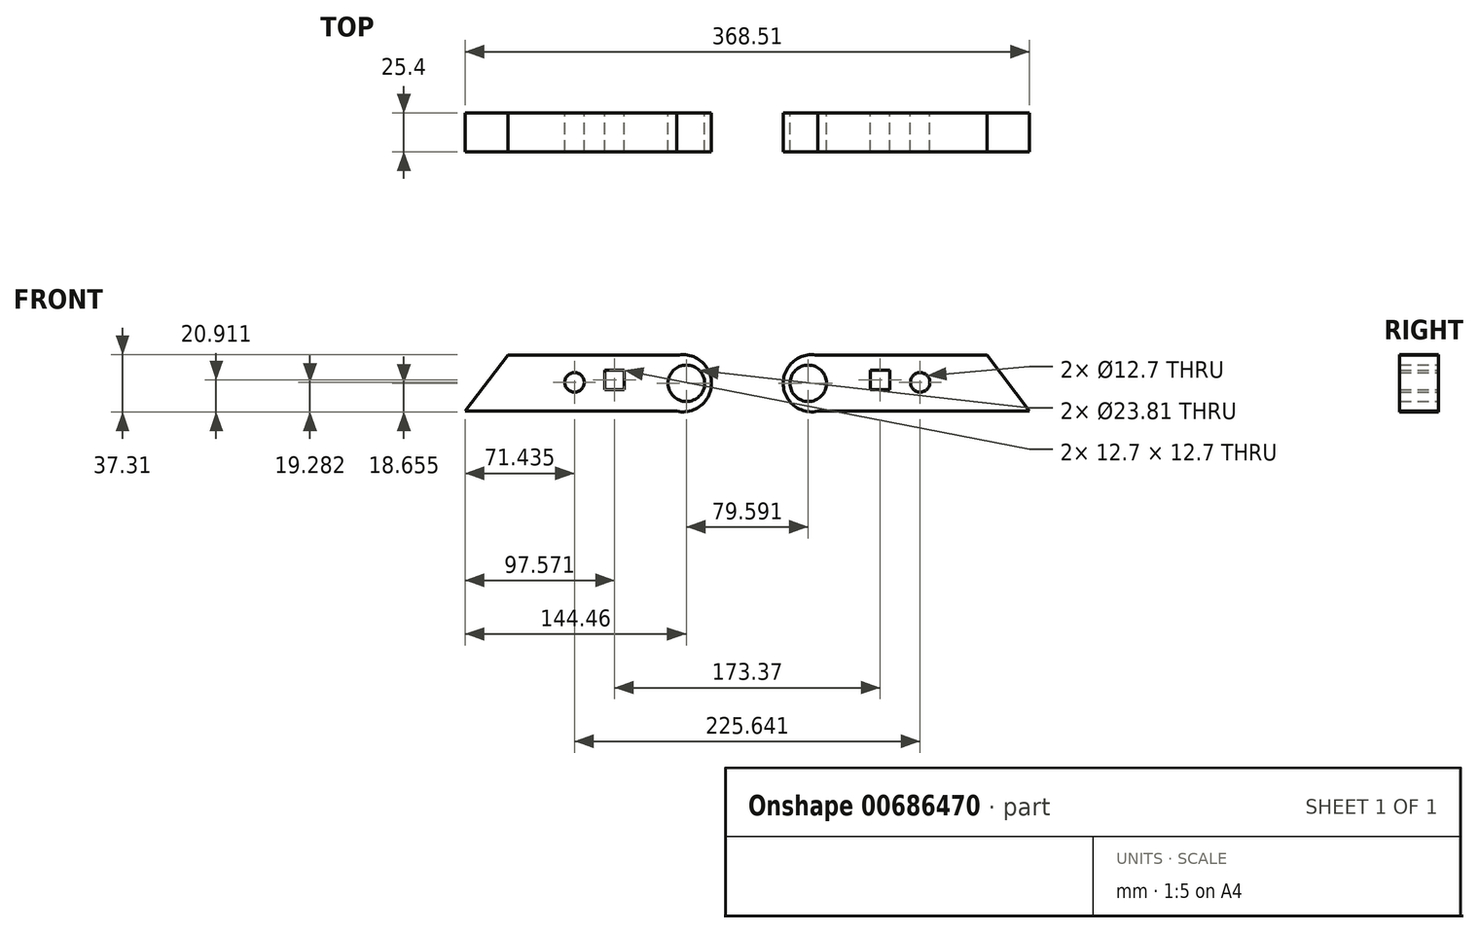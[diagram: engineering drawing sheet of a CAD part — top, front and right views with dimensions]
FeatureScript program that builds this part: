
annotation { "Feature Type Name" : "Feature", "Feature Type Description" : "" }
export const myFeature = defineFeature(function(context is Context, id is Id, definition is map)
    precondition{}
    {
        {
            var Q0;
            Q0=qCreatedBy(makeId("Front.planeOp"),FACE);
            var sketch = newSketch(context, id + "F0", { "sketchPlane" : qUnion([Q0])});
            skLineSegment(sketch, "E0", {"start": v(-48.92, 45.33) * mm, "end": v(61.5, 45.33) * mm});
            skLineSegment(sketch, "E1", {"start": v(-76.8, 8.82) * mm, "end": v(61.5, 8.82) * mm});
            skLineSegment(sketch, "E2", {"start": v(-48.92, 45.33) * mm, "end": v(-76.8, 8.82) * mm});
            skCircle(sketch, "E3", {"center": v(-5.36, 27.7) * mm, "radius": 6.35 * mm});
            skLineSegment(sketch, "E4.bottom", {"start": v(14.42, 35.68) * mm, "end": v(27.12, 35.68) * mm});
            skLineSegment(sketch, "E4.top", {"start": v(14.42, 22.98) * mm, "end": v(27.12, 22.98) * mm});
            skLineSegment(sketch, "E4.left", {"start": v(14.42, 35.68) * mm, "end": v(14.42, 22.98) * mm});
            skLineSegment(sketch, "E4.right", {"start": v(27.12, 35.68) * mm, "end": v(27.12, 22.98) * mm});
            skPoint(sketch, "E4.middle", {"position": v(20.77, 29.33) * mm});
            skCircle(sketch, "E5", {"center": v(67.66, 27.07) * mm, "radius": 11.9 * mm});
            skArc(sketch, "E6", {"start": v(61.5, 8.82) * mm, "mid": v(84.01, 27.07) * mm, "end": v(61.5, 45.33) * mm});
            skLineSegment(sketch, "E7", {"start": v(107.46, 0) * mm, "end": v(107.46, 77.52) * mm});
            skLineSegment(sketch, "E8.MirrorCS", {"start": v(263.83, 45.33) * mm, "end": v(153.4, 45.33) * mm});
            skArc(sketch, "E9.MirrorCS", {"start": v(153.4, 8.82) * mm, "mid": v(130.9, 27.07) * mm, "end": v(153.4, 45.33) * mm});
            skCircle(sketch, "E10.MirrorC", {"center": v(147.25, 27.07) * mm, "radius": 11.9 * mm});
            skLineSegment(sketch, "E11.MirrorCS", {"start": v(291.71, 8.82) * mm, "end": v(153.4, 8.82) * mm});
            skLineSegment(sketch, "E12.MirrorCS", {"start": v(200.5, 22.98) * mm, "end": v(187.8, 22.98) * mm});
            skLineSegment(sketch, "E13.MirrorCS", {"start": v(200.5, 35.68) * mm, "end": v(200.5, 22.98) * mm});
            skLineSegment(sketch, "E14.MirrorCS", {"start": v(200.5, 35.68) * mm, "end": v(187.8, 35.68) * mm});
            skLineSegment(sketch, "E15.MirrorCS", {"start": v(187.8, 35.68) * mm, "end": v(187.8, 22.98) * mm});
            skCircle(sketch, "E16.MirrorC", {"center": v(220.28, 27.7) * mm, "radius": 6.35 * mm});
            skLineSegment(sketch, "E17.MirrorCS", {"start": v(263.83, 45.33) * mm, "end": v(291.71, 8.82) * mm});
            skSolve(sketch);
        }
        {
            var Q0;
            Q0 = qSketchRegion(id + "F0", true);
            extrude(context, id + "F1", {"entities" : qUnion([Q0]), "depth" : 25.4 * mm, "offsetDistance" : 25.4 * mm});
        }
    });
